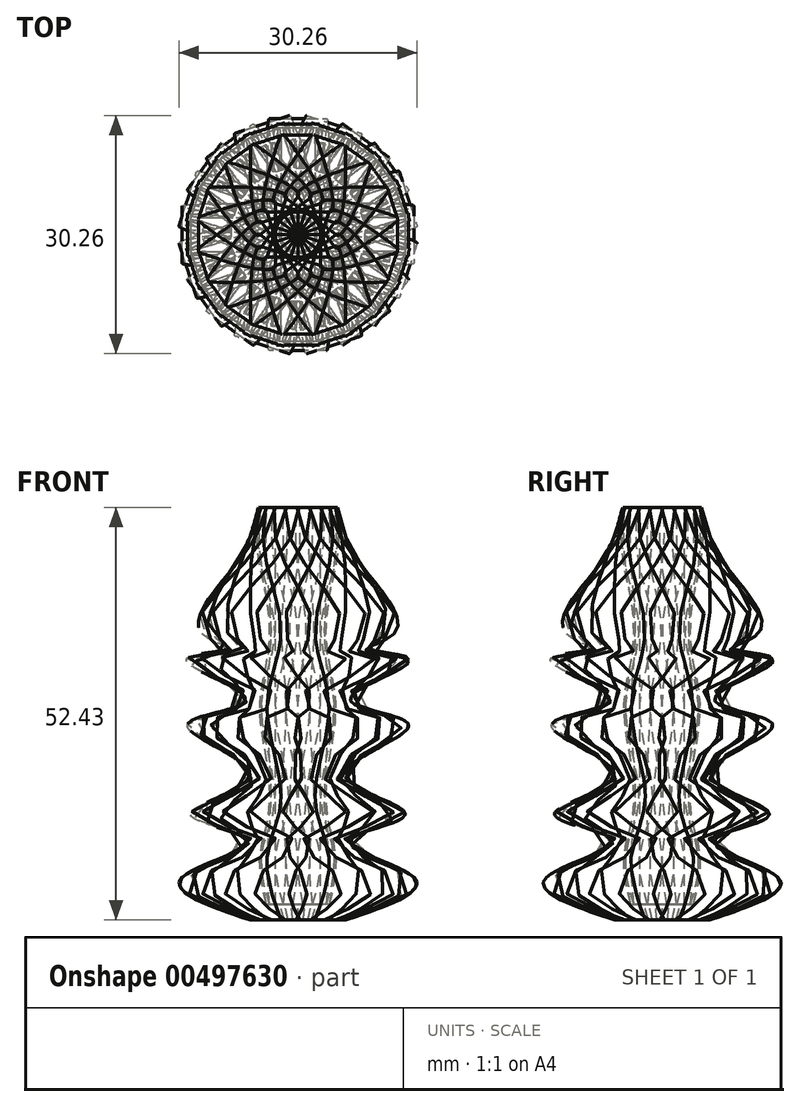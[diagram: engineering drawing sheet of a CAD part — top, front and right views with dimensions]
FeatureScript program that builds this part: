
annotation { "Feature Type Name" : "Feature", "Feature Type Description" : "" }
export const myFeature = defineFeature(function(context is Context, id is Id, definition is map)
    precondition{}
    {
        {
            var Q0;
            Q0=qCreatedBy(makeId("Front.planeOp"),FACE);
            var sketch = newSketch(context, id + "F0", { "sketchPlane" : qUnion([Q0])});
            skLineSegment(sketch, "E0", {"start": v(0, 0) * mm, "end": v(5.7, 0) * mm});
            skLineSegment(sketch, "E1.0", {"start": v(0, 2) * mm, "end": v(6.46, 2) * mm});
            skLineSegment(sketch, "E2", {"start": v(5.6, 59.97) * mm, "end": v(5.92, 59.97) * mm});
            skLineSegment(sketch, "E3", {"start": v(0, 2) * mm, "end": v(0, 0) * mm});
            skLineSegment(sketch, "E4", {"start": v(0, 0) * mm, "end": v(0, 15.37) * mm});
            skLineSegment(sketch, "E5", {"start": v(5.7, 36.68) * mm, "end": v(-2.4, 36.68) * mm});
            skPoint(sketch, "E6.11.internal.snap0", {"position": v(2.85, 0) * mm});
            skFitSpline(sketch, "E6", {"points": [v(5.7, 0) * mm, v(14.5, 5.16) * mm, v(5.7, 10) * mm, v(13.57, 13.46) * mm, v(5.7, 18.53) * mm, v(13.57, 24.76) * mm, v(5.7, 27.98) * mm, v(14.03, 33.06) * mm, v(8.5, 34.44) * mm, v(12.42, 36.75) * mm, v(5.7, 46.66) * mm, v(2.85, 52.43) * mm], "startDerivative": vector(153.62, 51.54) * mm, "endDerivative": vector(-17.26, 64.61) * mm});
            skLineSegment(sketch, "E7", {"start": v(2.85, 52.43) * mm, "end": v(2.85, 2) * mm});
            skSolve(sketch);
        }
        {
            var Q0;
            {var subQ5=sQuery(id+"F0.wireOp",EDGE,"E0");Q0=makeQuery(id+"F0.imprint","IMPRINT",FACE,{"disambiguationData":[TD([[makeQuery(id+"F0.imprint","IMPRINT",EDGE,{"derivedFrom":subQ5}),1.0]])]});}
            extrude(context, id + "F1", {"entities" : qUnion([Q0]), "depth" : 5 * mm, "hasSecondDirection" : true, "secondDirectionOppositeDirection" : true, "secondDirectionDepth" : 5 * mm});
        }
        {
            var Q0;
            Q0=qCreatedBy(makeId("Right.planeOp"),FACE);
            var sketch = newSketch(context, id + "F2", { "sketchPlane" : qUnion([Q0])});
            skLineSegment(sketch, "E8", {"start": v(0, 0) * mm, "end": v(-4.3, 0) * mm});
            skPoint(sketch, "E9.2.internal.snap0", {"position": v(-2.15, 0) * mm});
            skPoint(sketch, "E9.4.internal.snap0", {"position": v(-2.15, 0) * mm});
            skPoint(sketch, "E9.6.internal.snap0", {"position": v(-2.15, 0) * mm});
            skFitSpline(sketch, "E9", {"points": [v(-2.15, 0) * mm, v(-3.93, 8.1) * mm, v(-2.15, 15.32) * mm, v(-3.93, 27.02) * mm, v(-2.15, 36.73) * mm, v(-4.35, 47.38) * mm, v(-2.15, 60) * mm], "startDerivative": vector(-20.3, 55.55) * mm, "endDerivative": vector(20.8, 68.41) * mm});
            skLineSegment(sketch, "E10", {"start": v(0, 60) * mm, "end": v(-2.15, 60) * mm});
            skLineSegment(sketch, "E11", {"start": v(0, 60) * mm, "end": v(0, 0) * mm});
            skFitSpline(sketch, "E12.MirrorCS", {"points": [v(2.15, 0) * mm, v(3.93, 8.1) * mm, v(2.15, 15.32) * mm, v(3.93, 27.02) * mm, v(2.15, 36.73) * mm, v(4.35, 47.38) * mm, v(2.15, 60) * mm], "startDerivative": vector(20.3, 55.55) * mm, "endDerivative": vector(-20.8, 68.41) * mm});
            skLineSegment(sketch, "E13.MirrorCS", {"start": v(0, 0) * mm, "end": v(4.3, 0) * mm});
            skLineSegment(sketch, "E14.MirrorCS", {"start": v(0, 60) * mm, "end": v(2.15, 60) * mm});
            skSolve(sketch);
        }
        {
            var Q0;
            Q0=qSketchRegion(id+"F2",true);
            extrude(context, id + "F3", {"entities" : qUnion([Q0]), "operationType" : NewBodyOperationType.INTERSECT, "depth" : 25 * mm});
        }
        {
            var Q0;
            Q0=makeQuery(id+"F1.opExtrude","SWEPT_BODY",BODY,{"disambiguationData":[OSD([sQuery(id+"F0.wireOp",EDGE,"E0"),sQuery(id+"F0.wireOp",EDGE,"69a6ec41-09e3-4b96-a35e-9b828c85d251"),sQuery(id+"F0.wireOp",EDGE,"ce357062-ea5a-4ec7-b7ab-a59feb0f809f.0"),sQuery(id+"F0.wireOp",EDGE,"E1.0"),sQuery(id+"F0.wireOp",EDGE,"E2"),sQuery(id+"F0.wireOp",EDGE,"E4")])]});
            var Q1;
            Q1=sQuery(id+"F0.wireOp",EDGE,"E4");
            circularPattern(context, id + "F4", {"entities" : qUnion([Q0]), "axis" : qUnion([Q1]), "angle" : 360 * degree, "instanceCount" : 20, "equalSpace" : true});
        }
    });
